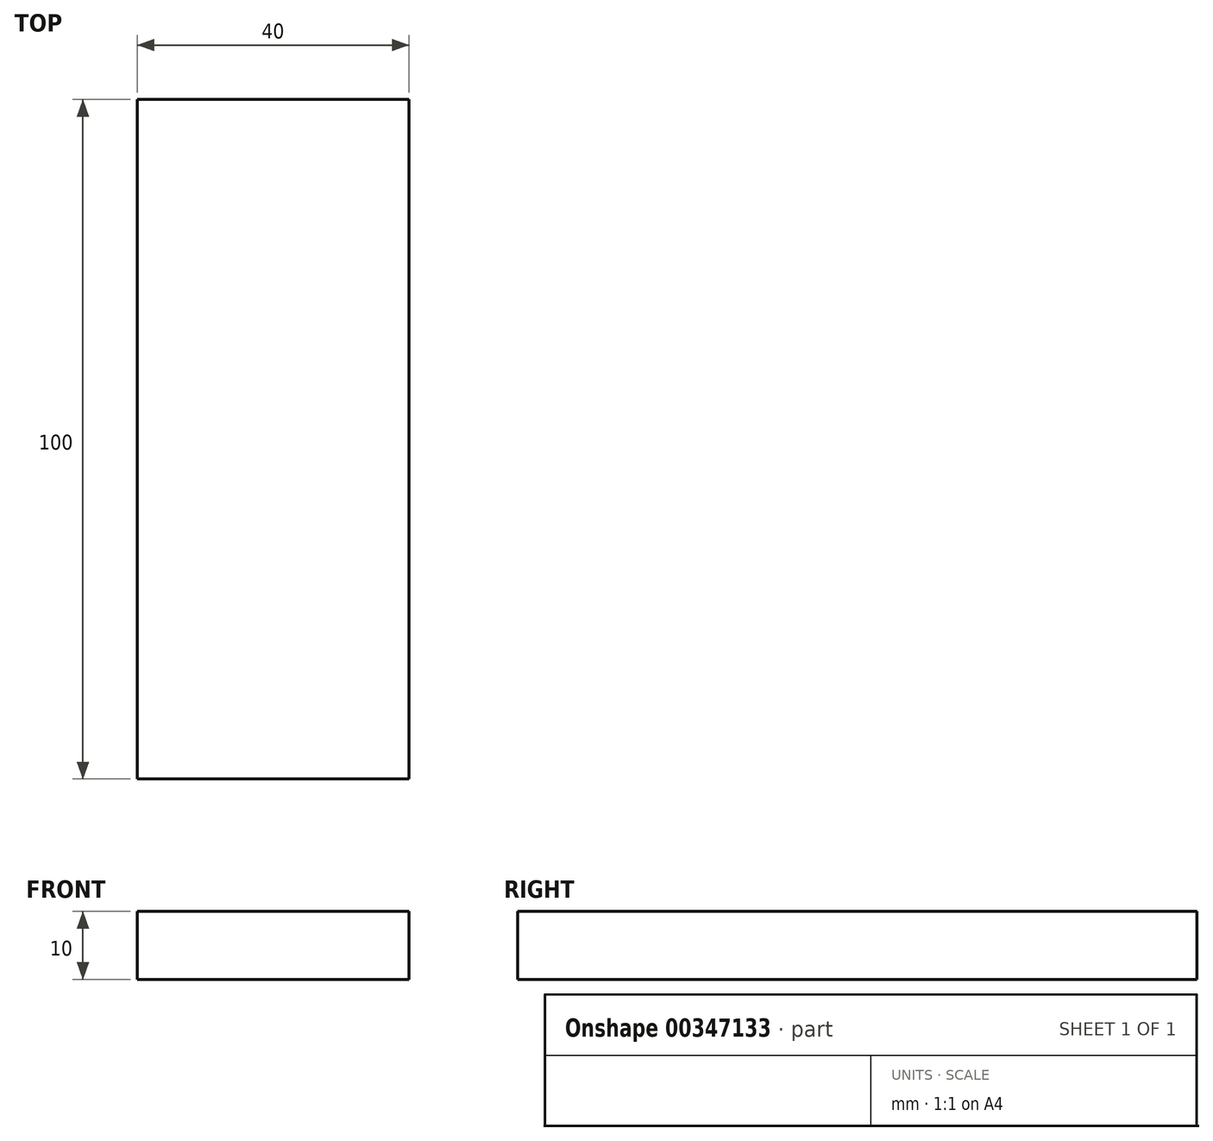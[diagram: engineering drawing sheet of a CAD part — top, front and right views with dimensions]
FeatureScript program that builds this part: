
annotation { "Feature Type Name" : "Feature", "Feature Type Description" : "" }
export const myFeature = defineFeature(function(context is Context, id is Id, definition is map)
    precondition{}
    {
        {
            var Q0;
            Q0=qCreatedBy(makeId("Top.planeOp"),FACE);
            var sketch = newSketch(context, id + "F0", { "sketchPlane" : qUnion([Q0])});
            skLineSegment(sketch, "E0.bottom", {"start": v(-20, 50) * mm, "end": v(20, 50) * mm});
            skLineSegment(sketch, "E0.top", {"start": v(-20, -50) * mm, "end": v(20, -50) * mm});
            skLineSegment(sketch, "E0.left", {"start": v(-20, 50) * mm, "end": v(-20, -50) * mm});
            skLineSegment(sketch, "E0.right", {"start": v(20, 50) * mm, "end": v(20, -50) * mm});
            skPoint(sketch, "E0.middle", {"position": v(0, 0) * mm});
            skPoint(sketch, "E1.visualSharp", {"position": v(-20, 50) * mm});
            skLineSegment(sketch, "E1.filletArc", {"start": v(-20, 50) * mm, "end": v(-20, 50) * mm});
            skPoint(sketch, "E2.visualSharp", {"position": v(20, 50) * mm});
            skLineSegment(sketch, "E2.filletArc", {"start": v(20, 50) * mm, "end": v(20, 50) * mm});
            skPoint(sketch, "E3.visualSharp", {"position": v(20, -50) * mm});
            skLineSegment(sketch, "E3.filletArc", {"start": v(20, -50) * mm, "end": v(20, -50) * mm});
            skPoint(sketch, "E4.visualSharp", {"position": v(-20, -50) * mm});
            skLineSegment(sketch, "E4.filletArc", {"start": v(-20, -50) * mm, "end": v(-20, -50) * mm});
            skSolve(sketch);
        }
        {
            var Q0;
            Q0=qSketchRegion(id+"F0",true);
            extrude(context, id + "F1", {"entities" : qUnion([Q0]), "depth" : 10 * mm});
        }
    });
